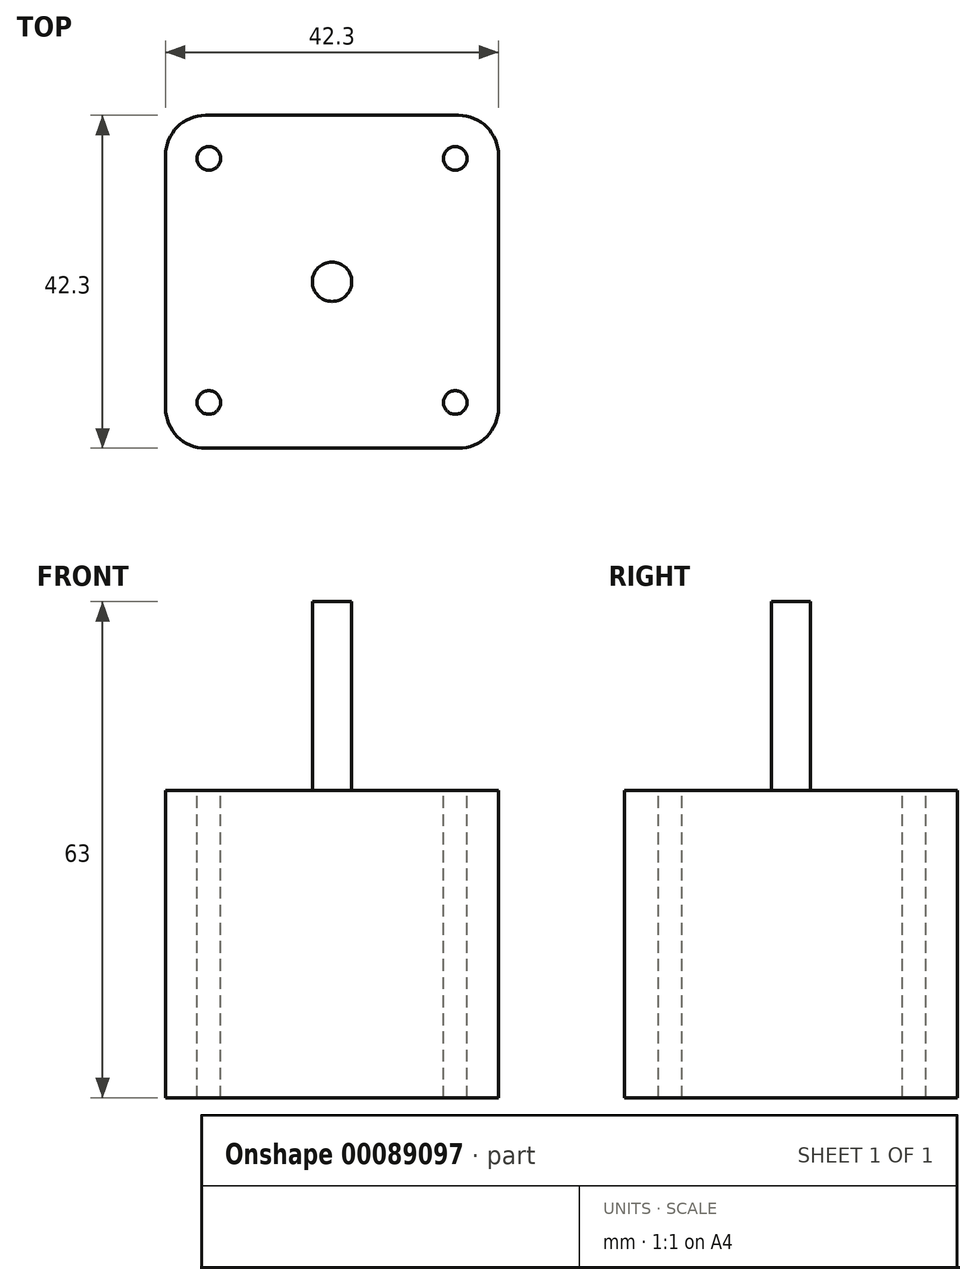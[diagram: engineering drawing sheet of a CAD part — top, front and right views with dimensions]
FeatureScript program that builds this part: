
annotation { "Feature Type Name" : "Feature", "Feature Type Description" : "" }
export const myFeature = defineFeature(function(context is Context, id is Id, definition is map)
    precondition{}
    {
        {
            var Q0;
            Q0=qCreatedBy(makeId("Top.planeOp"),FACE);
            var sketch = newSketch(context, id + "F0", { "sketchPlane" : qUnion([Q0])});
            skLineSegment(sketch, "E0.bottom", {"start": v(-21.43, 19.63) * mm, "end": v(20.87, 19.63) * mm});
            skLineSegment(sketch, "E0.top", {"start": v(-21.43, -22.67) * mm, "end": v(20.87, -22.67) * mm});
            skLineSegment(sketch, "E0.left", {"start": v(-21.43, 19.63) * mm, "end": v(-21.43, -22.67) * mm});
            skLineSegment(sketch, "E0.right", {"start": v(20.87, 19.63) * mm, "end": v(20.87, -22.67) * mm});
            skSolve(sketch);
        }
        {
            var Q0;
            Q0 = qSketchRegion(id + "F0", true);
            extrude(context, id + "F1", {"entities" : qUnion([Q0]), "depth" : 39 * mm});
        }
        {
            var Q0;
            Q0=makeQuery(id+"F1.opExtrude","SWEPT_EDGE",EDGE,{"disambiguationData":[OSD([sQuery(id+"F0.wireOp",EDGE,"E0.bottom"),sQuery(id+"F0.wireOp",EDGE,"E0.right")])]});
            var Q1;
            Q1=makeQuery(id+"F1.opExtrude","SWEPT_EDGE",EDGE,{"disambiguationData":[OSD([sQuery(id+"F0.wireOp",EDGE,"E0.top"),sQuery(id+"F0.wireOp",EDGE,"E0.right")])]});
            var Q2;
            Q2=makeQuery(id+"F1.opExtrude","SWEPT_EDGE",EDGE,{"disambiguationData":[OSD([sQuery(id+"F0.wireOp",EDGE,"E0.bottom"),sQuery(id+"F0.wireOp",EDGE,"E0.left")])]});
            var Q3;
            Q3=makeQuery(id+"F1.opExtrude","SWEPT_EDGE",EDGE,{"disambiguationData":[OSD([sQuery(id+"F0.wireOp",EDGE,"E0.top"),sQuery(id+"F0.wireOp",EDGE,"E0.left")])]});
            fillet(context, id + "F2", {"entities" : qUnion([Q0, Q1, Q2, Q3]), "radius" : 5.08 * mm, "tangentPropagation" : true, "allowEdgeOverflow" : false});
        }
        {
            var Q0;
            Q0=makeQuery(id+"F1.opExtrude","CAP_FACE",FACE,{"disambiguationData":[OSD([sQuery(id+"F0.wireOp",EDGE,"E0.bottom"),sQuery(id+"F0.wireOp",EDGE,"E0.top"),sQuery(id+"F0.wireOp",EDGE,"E0.left"),sQuery(id+"F0.wireOp",EDGE,"E0.right")])],"isStart":false});
            var sketch = newSketch(context, id + "F3", { "sketchPlane" : qUnion([Q0])});
            skPoint(sketch, "E1", {"position": v(15.37, 14.15) * mm});
            skPoint(sketch, "E2", {"position": v(15.37, -16.85) * mm});
            skLineSegment(sketch, "E3", {"start": v(-0.28, -23.44) * mm, "end": v(-0.28, 19.63) * mm});
            skPoint(sketch, "E3.startSnap0", {"position": v(-0.28, 19.63) * mm});
            skPoint(sketch, "E4.MirrorP", {"position": v(-15.93, 14.15) * mm});
            skPoint(sketch, "E5.MirrorP", {"position": v(-15.93, -16.85) * mm});
            skSolve(sketch);
        }
        {
            var Q0;
            Q0=sQuery(id+"F3.wireOp",VERTEX,"E1");
            var Q1;
            Q1=sQuery(id+"F3.wireOp",VERTEX,"E2");
            var Q2;
            Q2=sQuery(id+"F3.wireOp",VERTEX,"E5.MirrorP");
            var Q3;
            Q3=sQuery(id+"F3.wireOp",VERTEX,"E4.MirrorP");
            var Q4;
            Q4=makeQuery(id+"F1.opExtrude","SWEPT_BODY",BODY,{"disambiguationData":[OSD([sQuery(id+"F0.wireOp",EDGE,"E0.bottom"),sQuery(id+"F0.wireOp",EDGE,"E0.top"),sQuery(id+"F0.wireOp",EDGE,"E0.left"),sQuery(id+"F0.wireOp",EDGE,"E0.right")])]});
            hole(context, id + "F4", {"style" : HoleStyle.SIMPLE, "endStyle" : HoleEndStyle.THROUGH, "holeDiameter" : 3 * mm, "locations" : qUnion([Q0, Q1, Q2, Q3]), "scope" : qUnion([Q4]), "isTappedThrough" : true});
        }
        {
            var Q0;
            Q0=makeQuery(id+"F1.opExtrude","CAP_FACE",FACE,{"disambiguationData":[OSD([sQuery(id+"F0.wireOp",EDGE,"E0.bottom"),sQuery(id+"F0.wireOp",EDGE,"E0.top"),sQuery(id+"F0.wireOp",EDGE,"E0.left"),sQuery(id+"F0.wireOp",EDGE,"E0.right")])],"isStart":false});
            var sketch = newSketch(context, id + "F5", { "sketchPlane" : qUnion([Q0])});
            skLineSegment(sketch, "E6", {"start": v(20.87, -1.52) * mm, "end": v(-21.43, -1.52) * mm});
            skLineSegment(sketch, "E7", {"start": v(-0.28, 19.63) * mm, "end": v(-0.28, -22.67) * mm});
            skCircle(sketch, "E8", {"center": v(-0.28, -1.52) * mm, "radius": 2.5 * mm});
            skSolve(sketch);
        }
        {
            var Q0;
            Q0 = qSketchRegion(id + "F5", true);
            extrude(context, id + "F6", {"entities" : qUnion([Q0]), "operationType" : NewBodyOperationType.ADD, "depth" : 24 * mm});
        }
    });
